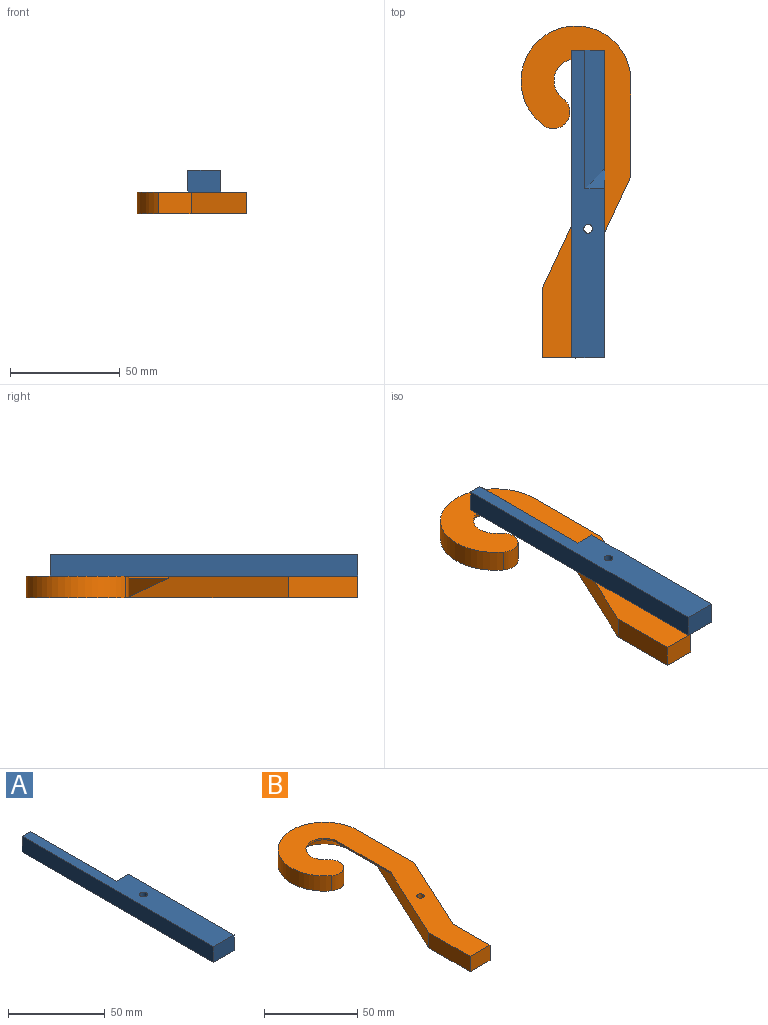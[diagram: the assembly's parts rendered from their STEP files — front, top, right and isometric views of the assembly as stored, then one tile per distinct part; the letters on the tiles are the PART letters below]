
ASSEMBLY  parts=2 mates=1
PART A: 9 faces, bbox 15x140x10 mm
  f0: plane 140x10mm, normal (-1,0,0), area 1400mm2, adj f1,f4,f5,f6
  f1: plane 15x10mm, normal (0,-1,0), area 150mm2, adj f0,f2,f4,f5
  f2: plane 140x10mm, normal (1,0,0), area 873.4mm2, adj f1,f4,f5,f6,f7,f8
  f3: cylinder r=2mm len=10mm, axis (0,0,-1), area 125.7mm2, adj f4,f5
  f4: plane 140x15mm, normal (0,0,1), area 1520.3mm2, adj f0,f1,f2,f3,f6,f7,f8
  f5: plane 140x15mm, normal (0,0,-1), area 2087.4mm2, adj f0,f1,f2,f3,f6
  f6: plane 15x10mm, normal (0,1,0), area 109.5mm2, adj f0,f2,f4,f5,f7
  f7: plane 63.01x9mm, normal (0.71,0,0.71), area 744.7mm2, adj f2,f4,f6,f8
  f8: plane 9x9mm, normal (0,0.71,0.71), area 57.3mm2, adj f2,f4,f7
PART B: 15 faces, bbox 50x151x10 mm
  f0: cylinder r=25mm len=50mm, axis (0,0,-1), area 1019.1mm2, adj f1,f9,f11,f12
  f1: cylinder r=7.5mm len=15mm, axis (0,0,-1), area 301.1mm2, adj f0,f2,f11,f12,f13
  f2: cylinder r=10mm len=20mm, axis (0,0,-1), area 40.8mm2, adj f1,f3,f11,f13
  f3: plane 40x1mm, normal (-1,0,0), area 40mm2, adj f2,f4,f11,f14
  f4: plane 73.68x34.36mm, normal (-0.91,0.42,0), area 695.8mm2, adj f3,f5,f11,f12,f14
  f5: plane 31.61x10mm, normal (-1,0,0), area 316.1mm2, adj f4,f6,f11,f12
  f6: plane 15x10mm, normal (0,-1,0), area 150mm2, adj f5,f7,f11,f12
  f7: plane 28.28x10mm, normal (1,0,0), area 282.8mm2, adj f6,f8,f11,f12
  f8: plane 54.38x25.36mm, normal (0.91,-0.42,0), area 600mm2, adj f7,f9,f11,f12
  f9: plane 43.33x10mm, normal (1,0,0), area 433.3mm2, adj f0,f8,f11,f12
  f10: cylinder r=2mm len=10mm, axis (0,0,-1), area 125.7mm2, adj f11,f12
  f11: plane 150.99x50mm, normal (0,0,1), area 3122.8mm2, adj f0,f1,f2,f3,f4,f5,f6,f7
  f12: plane 150.99x50mm, normal (0,0,-1), area 2368mm2, adj f0,f1,f4,f5,f6,f7,f8,f9
  f13: cone r=19mm half-angle=45deg, axis (0,0,-1), area 681.2mm2, adj f1,f2,f12,f14
  f14: plane 40x9mm, normal (-0.71,0,-0.71), area 386.3mm2, adj f3,f4,f12,f13
PLACE A t=(-26.76,28.2,-8.3)mm
PLACE B rot(axis=(0,0,-1),0deg) t=(-26.73,28.2,-8.3)mm
MATE revolute B.f10 <-> A.f3  axis (0,0,-1) through (-38.7,-24.06,1.7)mm
